# Revit family: 4C-15_Door_High_Units_FL.rfa
name_source: partatom
category: Specialty Equipment
revit_build: Autodesk Revit 2016 (Build: 20150714_1515(x64)
units: mm (PartAtom-declared; Revit-internal decimal feet)

## family parameters
Always vertical = Yes
Cut with Voids When Loaded = No
Host = Wall
Part Type = Normal
Room Calculation Point = No
Round Connector Dimension = Use Diameter
Shared = No

## types (20) — shared parameters
Assembly Code = C1030910
Back Enclosure Material = Aluminum - Salsbury Finish = Anodized
Depth = 17.025"
Height = 54.970"
Latch Locks - Left Side = No
Latch Locks - Right Side = No
Lock Material = Stainless Steel -Salsbury Finish =  Polished
Manufacturer = Salsbury Industries
MasterFormat Number = 10 55 00
MasterFormat Title = Postal Specialties
Version = 2.0 (08/09/16)

## per-type parameters (varying)
- 3715S-09 FL: Bottom Back Plate=No; Description=15 Door High Unit: 9 MB1, 1 PL4, OM2; Door Slot L1=3700 Series 4C Door Configurations : Empty; Door Slot L10=3700 Series 4C Door Configurations : Empty; Door Slot L11=3700 Series 4C Door Configurations : Empty; Door Slot L12=3700 Series 4C Door Configurations : Empty; Door Slot L13=3700 Series 4C Door Configurations : Empty; Door Slot L14=3700 Series 4C Door Configurations : Empty; Door Slot L15=3700 Series 4C Door Configurations : Empty; Door Slot L2=3700 Series 4C Door Configurations : Empty; Door Slot L3=3700 Series 4C Door Configurations : Empty; Door Slot L4=3700 Series 4C Door Configurations : Empty; Door Slot L5=3700 Series 4C Door Configurations : Empty; Door Slot L6=3700 Series 4C Door Configurations : Empty; Door Slot L7=3700 Series 4C Door Configurations : Empty; Door Slot L8=3700 Series 4C Door Configurations : Empty; Door Slot L9=3700 Series 4C Door Configurations : Empty; Door Slot R1=3700 Series 4C Door Configurations : MB1 Door; Door Slot R10=3700 Series 4C Door Configurations : MB1 Door w/ Divider; Door Slot R11=3700 Series 4C Door Configurations : MB1 Door w/ Divider; Door Slot R12=3700 Series 4C Door Configurations : Empty; Door Slot R13=3700 Series 4C Door Configurations : Empty; Door Slot R14=3700 Series 4C Door Configurations : Empty; Door Slot R15=3700 Series 4C Parcel Configurations : PL4 w/ Divider; Door Slot R2=3700 Series 4C Door Configurations : MB1 Door w/ Divider; Door Slot R3=3700 Series 4C Door Configurations : MB1 Door w/ Divider; Door Slot R4=3700 Series 4C Door Configurations : MB1 Door w/ Divider; Door Slot R5=3700 Series 4C Door Configurations : MB1 Door w/ Divider; Door Slot R6=3700 Series 4C Door Configurations : Empty; Door Slot R7=3700 Series 4C OM2 Configuration : OM2-FL; Door Slot R8=3700 Series 4C Door Configurations : MB1 Door w/ Divider; Door Slot R9=3700 Series 4C Door Configurations : MB1 Door w/ Divider; Latch Alignment=13.876"; Left Inside Wall=No; Right Inside Wall=No; Top Back Plate=No; Type Comments=4C Standard Horizontal Mailbox - Front Loading; Vertical Center Divider=No; Width=16.344"
- 3715D-20 FL: Bottom Back Plate=Yes; Description=15 Door High Unit: 20 MB1, 2 PL4, OM2; Door Slot L1=3700 Series 4C Door Configurations : MB1 Door; Door Slot L10=3700 Series 4C Door Configurations : MB1 Door w/ Divider; Door Slot L11=3700 Series 4C Door Configurations : MB1 Door w/ Divider; Door Slot L12=3700 Series 4C Door Configurations : Empty; Door Slot L13=3700 Series 4C Door Configurations : Empty; Door Slot L14=3700 Series 4C Door Configurations : Empty; Door Slot L15=3700 Series 4C Parcel Configurations : PL4 w/ Divider; Door Slot L2=3700 Series 4C Door Configurations : MB1 Door w/ Divider; Door Slot L3=3700 Series 4C Door Configurations : MB1 Door w/ Divider; Door Slot L4=3700 Series 4C Door Configurations : MB1 Door w/ Divider; Door Slot L5=3700 Series 4C Door Configurations : MB1 Door w/ Divider; Door Slot L6=3700 Series 4C Door Configurations : MB1 Door w/ Divider; Door Slot L7=3700 Series 4C Door Configurations : MB1 Door w/ Divider; Door Slot L8=3700 Series 4C Door Configurations : MB1 Door w/ Divider; Door Slot L9=3700 Series 4C Door Configurations : MB1 Door w/ Divider; Door Slot R1=3700 Series 4C Door Configurations : MB1 Door; Door Slot R10=3700 Series 4C Door Configurations : MB1 Door w/ Divider; Door Slot R11=3700 Series 4C Door Configurations : MB1 Door w/ Divider; Door Slot R12=3700 Series 4C Door Configurations : Empty; Door Slot R13=3700 Series 4C Door Configurations : Empty; Door Slot R14=3700 Series 4C Door Configurations : Empty; Door Slot R15=3700 Series 4C Parcel Configurations : PL4 w/ Divider; Door Slot R2=3700 Series 4C Door Configurations : MB1 Door w/ Divider; Door Slot R3=3700 Series 4C Door Configurations : MB1 Door w/ Divider; Door Slot R4=3700 Series 4C Door Configurations : MB1 Door w/ Divider; Door Slot R5=3700 Series 4C Door Configurations : MB1 Door w/ Divider; Door Slot R6=3700 Series 4C Door Configurations : Empty; Door Slot R7=3700 Series 4C OM2 Configuration : OM2-FL; Door Slot R8=3700 Series 4C Door Configurations : MB1 Door w/ Divider; Door Slot R9=3700 Series 4C Door Configurations : MB1 Door w/ Divider; Latch Alignment=14.857"; Left Inside Wall=Yes; Right Inside Wall=Yes; Top Back Plate=Yes; Type Comments=4C Standard Horizontal Mailbox - Front Loading; Vertical Center Divider=Yes; Width=31.098"
- 3715D-19 FL: Bottom Back Plate=Yes; Description=15 Door High Unit: 19 MB1, 1 PL4, 1 PL5, OM2; Door Slot L1=3700 Series 4C Door Configurations : MB1 Door; Door Slot L10=3700 Series 4C Door Configurations : MB1 Door w/ Divider; Door Slot L11=3700 Series 4C Door Configurations : Empty; Door Slot L12=3700 Series 4C Door Configurations : Empty; Door Slot L13=3700 Series 4C Door Configurations : Empty; Door Slot L14=3700 Series 4C Door Configurations : Empty; Door Slot L15=3700 Series 4C Parcel Configurations : PL5 w/ Divider; Door Slot L2=3700 Series 4C Door Configurations : MB1 Door w/ Divider; Door Slot L3=3700 Series 4C Door Configurations : MB1 Door w/ Divider; Door Slot L4=3700 Series 4C Door Configurations : MB1 Door w/ Divider; Door Slot L5=3700 Series 4C Door Configurations : MB1 Door w/ Divider; Door Slot L6=3700 Series 4C Door Configurations : MB1 Door w/ Divider; Door Slot L7=3700 Series 4C Door Configurations : MB1 Door w/ Divider; Door Slot L8=3700 Series 4C Door Configurations : MB1 Door w/ Divider; Door Slot L9=3700 Series 4C Door Configurations : MB1 Door w/ Divider; Door Slot R1=3700 Series 4C Door Configurations : MB1 Door; Door Slot R10=3700 Series 4C Door Configurations : MB1 Door w/ Divider; Door Slot R11=3700 Series 4C Door Configurations : MB1 Door w/ Divider; Door Slot R12=3700 Series 4C Door Configurations : Empty; Door Slot R13=3700 Series 4C Door Configurations : Empty; Door Slot R14=3700 Series 4C Door Configurations : Empty; Door Slot R15=3700 Series 4C Parcel Configurations : PL4 w/ Divider; Door Slot R2=3700 Series 4C Door Configurations : MB1 Door w/ Divider; Door Slot R3=3700 Series 4C Door Configurations : MB1 Door w/ Divider; Door Slot R4=3700 Series 4C Door Configurations : MB1 Door w/ Divider; Door Slot R5=3700 Series 4C Door Configurations : MB1 Door w/ Divider; Door Slot R6=3700 Series 4C Door Configurations : Empty; Door Slot R7=3700 Series 4C OM2 Configuration : OM2-FL; Door Slot R8=3700 Series 4C Door Configurations : MB1 Door w/ Divider; Door Slot R9=3700 Series 4C Door Configurations : MB1 Door w/ Divider; Latch Alignment=14.857"; Left Inside Wall=Yes; Right Inside Wall=Yes; Top Back Plate=Yes; Type Comments=4C Standard Horizontal Mailbox - Front Loading; Vertical Center Divider=Yes; Width=31.098"
- 3715D-18 FL: Bottom Back Plate=Yes; Description=15 Door High Unit: 18 MB1, 2 PL5, OM2; Door Slot L1=3700 Series 4C Door Configurations : MB1 Door; Door Slot L10=3700 Series 4C Door Configurations : MB1 Door w/ Divider; Door Slot L11=3700 Series 4C Door Configurations : Empty; Door Slot L12=3700 Series 4C Door Configurations : Empty; Door Slot L13=3700 Series 4C Door Configurations : Empty; Door Slot L14=3700 Series 4C Door Configurations : Empty; Door Slot L15=3700 Series 4C Parcel Configurations : PL5 w/ Divider; Door Slot L2=3700 Series 4C Door Configurations : MB1 Door w/ Divider; Door Slot L3=3700 Series 4C Door Configurations : MB1 Door w/ Divider; Door Slot L4=3700 Series 4C Door Configurations : MB1 Door w/ Divider; Door Slot L5=3700 Series 4C Door Configurations : MB1 Door w/ Divider; Door Slot L6=3700 Series 4C Door Configurations : MB1 Door w/ Divider; Door Slot L7=3700 Series 4C Door Configurations : MB1 Door w/ Divider; Door Slot L8=3700 Series 4C Door Configurations : MB1 Door w/ Divider; Door Slot L9=3700 Series 4C Door Configurations : MB1 Door w/ Divider; Door Slot R1=3700 Series 4C Door Configurations : MB1 Door; Door Slot R10=3700 Series 4C Door Configurations : MB1 Door w/ Divider; Door Slot R11=3700 Series 4C Door Configurations : Empty; Door Slot R12=3700 Series 4C Door Configurations : Empty; Door Slot R13=3700 Series 4C Door Configurations : Empty; Door Slot R14=3700 Series 4C Door Configurations : Empty; Door Slot R15=3700 Series 4C Parcel Configurations : PL5 w/ Divider; Door Slot R2=3700 Series 4C Door Configurations : MB1 Door w/ Divider; Door Slot R3=3700 Series 4C Door Configurations : MB1 Door w/ Divider; Door Slot R4=3700 Series 4C Door Configurations : MB1 Door w/ Divider; Door Slot R5=3700 Series 4C Door Configurations : MB1 Door w/ Divider; Door Slot R6=3700 Series 4C Door Configurations : Empty; Door Slot R7=3700 Series 4C OM2 Configuration : OM2-FL; Door Slot R8=3700 Series 4C Door Configurations : MB1 Door w/ Divider; Door Slot R9=3700 Series 4C Door Configurations : MB1 Door w/ Divider; Latch Alignment=14.857"; Left Inside Wall=Yes; Right Inside Wall=Yes; Top Back Plate=Yes; Type Comments=4C Standard Horizontal Mailbox - Front Loading; Vertical Center Divider=Yes; Width=31.098"
- 3715D-17 FL: Bottom Back Plate=Yes; Description=15 Door High Unit: 17 MB1, 1 PL5, 1 PL6, OM2; Door Slot L1=3700 Series 4C Door Configurations : MB1 Door; Door Slot L10=3700 Series 4C Door Configurations : Empty; Door Slot L11=3700 Series 4C Door Configurations : Empty; Door Slot L12=3700 Series 4C Door Configurations : Empty; Door Slot L13=3700 Series 4C Door Configurations : Empty; Door Slot L14=3700 Series 4C Door Configurations : Empty; Door Slot L15=3700 Series 4C Parcel Configurations : PL6 w/ Divider; Door Slot L2=3700 Series 4C Door Configurations : MB1 Door w/ Divider; Door Slot L3=3700 Series 4C Door Configurations : MB1 Door w/ Divider; Door Slot L4=3700 Series 4C Door Configurations : MB1 Door w/ Divider; Door Slot L5=3700 Series 4C Door Configurations : MB1 Door w/ Divider; Door Slot L6=3700 Series 4C Door Configurations : MB1 Door w/ Divider; Door Slot L7=3700 Series 4C Door Configurations : MB1 Door w/ Divider; Door Slot L8=3700 Series 4C Door Configurations : MB1 Door w/ Divider; Door Slot L9=3700 Series 4C Door Configurations : MB1 Door w/ Divider; Door Slot R1=3700 Series 4C Door Configurations : MB1 Door; Door Slot R10=3700 Series 4C Door Configurations : MB1 Door w/ Divider; Door Slot R11=3700 Series 4C Door Configurations : Empty; Door Slot R12=3700 Series 4C Door Configurations : Empty; Door Slot R13=3700 Series 4C Door Configurations : Empty; Door Slot R14=3700 Series 4C Door Configurations : Empty; Door Slot R15=3700 Series 4C Parcel Configurations : PL5 w/ Divider; Door Slot R2=3700 Series 4C Door Configurations : MB1 Door w/ Divider; Door Slot R3=3700 Series 4C Door Configurations : MB1 Door w/ Divider; Door Slot R4=3700 Series 4C Door Configurations : MB1 Door w/ Divider; Door Slot R5=3700 Series 4C Door Configurations : MB1 Door w/ Divider; Door Slot R6=3700 Series 4C Door Configurations : Empty; Door Slot R7=3700 Series 4C OM2 Configuration : OM2-FL; Door Slot R8=3700 Series 4C Door Configurations : MB1 Door w/ Divider; Door Slot R9=3700 Series 4C Door Configurations : MB1 Door w/ Divider; Latch Alignment=14.857"; Left Inside Wall=Yes; Right Inside Wall=Yes; Top Back Plate=Yes; Type Comments=4C Standard Horizontal Mailbox - Front Loading; Vertical Center Divider=Yes; Width=31.098"
- 3715D-16 FL: Bottom Back Plate=Yes; Description=15 Door High Unit: 16 MB1, 2 PL6, OM2; Door Slot L1=3700 Series 4C Door Configurations : MB1 Door; Door Slot L10=3700 Series 4C Door Configurations : Empty; Door Slot L11=3700 Series 4C Door Configurations : Empty; Door Slot L12=3700 Series 4C Door Configurations : Empty; Door Slot L13=3700 Series 4C Door Configurations : Empty; Door Slot L14=3700 Series 4C Door Configurations : Empty; Door Slot L15=3700 Series 4C Parcel Configurations : PL6 w/ Divider; Door Slot L2=3700 Series 4C Door Configurations : MB1 Door w/ Divider; Door Slot L3=3700 Series 4C Door Configurations : MB1 Door w/ Divider; Door Slot L4=3700 Series 4C Door Configurations : MB1 Door w/ Divider; Door Slot L5=3700 Series 4C Door Configurations : MB1 Door w/ Divider; Door Slot L6=3700 Series 4C Door Configurations : MB1 Door w/ Divider; Door Slot L7=3700 Series 4C Door Configurations : MB1 Door w/ Divider; Door Slot L8=3700 Series 4C Door Configurations : MB1 Door w/ Divider; Door Slot L9=3700 Series 4C Door Configurations : MB1 Door w/ Divider; Door Slot R1=3700 Series 4C Door Configurations : MB1 Door; Door Slot R10=3700 Series 4C Door Configurations : Empty; Door Slot R11=3700 Series 4C Door Configurations : Empty; Door Slot R12=3700 Series 4C Door Configurations : Empty; Door Slot R13=3700 Series 4C Door Configurations : Empty; Door Slot R14=3700 Series 4C Door Configurations : Empty; Door Slot R15=3700 Series 4C Parcel Configurations : PL6 w/ Divider; Door Slot R2=3700 Series 4C Door Configurations : MB1 Door w/ Divider; Door Slot R3=3700 Series 4C Door Configurations : MB1 Door w/ Divider; Door Slot R4=3700 Series 4C Door Configurations : MB1 Door w/ Divider; Door Slot R5=3700 Series 4C Door Configurations : MB1 Door w/ Divider; Door Slot R6=3700 Series 4C Door Configurations : Empty; Door Slot R7=3700 Series 4C OM2 Configuration : OM2-FL; Door Slot R8=3700 Series 4C Door Configurations : MB1 Door w/ Divider; Door Slot R9=3700 Series 4C Door Configurations : MB1 Door w/ Divider; Latch Alignment=14.857"; Left Inside Wall=Yes; Right Inside Wall=Yes; Top Back Plate=Yes; Type Comments=4C Standard Horizontal Mailbox - Front Loading; Vertical Center Divider=Yes; Width=31.098"
- 3715D-15 FL: Bottom Back Plate=Yes; Description=15 Door High Unit: 15 MB1, 2 PL6, OM3; Door Slot L1=3700 Series 4C Door Configurations : MB1 Door; Door Slot L10=3700 Series 4C Door Configurations : Empty; Door Slot L11=3700 Series 4C Door Configurations : Empty; Door Slot L12=3700 Series 4C Door Configurations : Empty; Door Slot L13=3700 Series 4C Door Configurations : Empty; Door Slot L14=3700 Series 4C Door Configurations : Empty; Door Slot L15=3700 Series 4C Parcel Configurations : PL6 w/ Divider; Door Slot L2=3700 Series 4C Door Configurations : MB1 Door w/ Divider; Door Slot L3=3700 Series 4C Door Configurations : MB1 Door w/ Divider; Door Slot L4=3700 Series 4C Door Configurations : MB1 Door w/ Divider; Door Slot L5=3700 Series 4C Door Configurations : MB1 Door w/ Divider; Door Slot L6=3700 Series 4C Door Configurations : MB1 Door w/ Divider; Door Slot L7=3700 Series 4C Door Configurations : MB1 Door w/ Divider; Door Slot L8=3700 Series 4C Door Configurations : MB1 Door w/ Divider; Door Slot L9=3700 Series 4C Door Configurations : MB1 Door w/ Divider; Door Slot R1=3700 Series 4C Door Configurations : MB1 Door; Door Slot R10=3700 Series 4C Door Configurations : Empty; Door Slot R11=3700 Series 4C Door Configurations : Empty; Door Slot R12=3700 Series 4C Door Configurations : Empty; Door Slot R13=3700 Series 4C Door Configurations : Empty; Door Slot R14=3700 Series 4C Door Configurations : Empty; Door Slot R15=3700 Series 4C Parcel Configurations : PL6 w/ Divider; Door Slot R2=3700 Series 4C Door Configurations : MB1 Door w/ Divider; Door Slot R3=3700 Series 4C Door Configurations : MB1 Door w/ Divider; Door Slot R4=3700 Series 4C Door Configurations : MB1 Door w/ Divider; Door Slot R5=3700 Series 4C Door Configurations : MB1 Door w/ Divider; Door Slot R6=3700 Series 4C Door Configurations : Empty; Door Slot R7=3700 Series 4C Door Configurations : Empty; Door Slot R8=3700 Series 4C OM3 Configuration : OM3-FL; Door Slot R9=3700 Series 4C Door Configurations : MB1 Door w/ Divider; Latch Alignment=14.857"; Left Inside Wall=Yes; Right Inside Wall=Yes; Top Back Plate=Yes; Type Comments=4C Standard Horizontal Mailbox - Front Loading; Vertical Center Divider=Yes; Width=31.098"
- 3715D-09 FL: Bottom Back Plate=Yes; Description=15 Door High Unit: 9 MB2, 2 PL5, OM2; Door Slot L1=3700 Series 4C Door Configurations : Empty; Door Slot L10=3700 Series 4C Door Configurations : MB2 Door w/ Divider; Door Slot L11=3700 Series 4C Door Configurations : Empty; Door Slot L12=3700 Series 4C Door Configurations : Empty; Door Slot L13=3700 Series 4C Door Configurations : Empty; Door Slot L14=3700 Series 4C Door Configurations : Empty; Door Slot L15=3700 Series 4C Parcel Configurations : PL5 w/ Divider; Door Slot L2=3700 Series 4C Door Configurations : MB2 Door; Door Slot L3=3700 Series 4C Door Configurations : Empty; Door Slot L4=3700 Series 4C Door Configurations : MB2 Door w/ Divider; Door Slot L5=3700 Series 4C Door Configurations : Empty; Door Slot L6=3700 Series 4C Door Configurations : MB2 Door w/ Divider; Door Slot L7=3700 Series 4C Door Configurations : Empty; Door Slot L8=3700 Series 4C Door Configurations : MB2 Door w/ Divider; Door Slot L9=3700 Series 4C Door Configurations : Empty; Door Slot R1=3700 Series 4C Door Configurations : Empty; Door Slot R10=3700 Series 4C Door Configurations : MB2 Door w/ Divider; Door Slot R11=3700 Series 4C Door Configurations : Empty; Door Slot R12=3700 Series 4C Door Configurations : Empty; Door Slot R13=3700 Series 4C Door Configurations : Empty; Door Slot R14=3700 Series 4C Door Configurations : Empty; Door Slot R15=3700 Series 4C Parcel Configurations : PL5 w/ Divider; Door Slot R2=3700 Series 4C Door Configurations : MB2 Door; Door Slot R3=3700 Series 4C Door Configurations : Empty; Door Slot R4=3700 Series 4C Door Configurations : MB2 Door w/ Divider; Door Slot R5=3700 Series 4C Door Configurations : Empty; Door Slot R6=3700 Series 4C Door Configurations : MB2 Door w/ Divider; Door Slot R7=3700 Series 4C Door Configurations : Empty; Door Slot R8=3700 Series 4C OM2 Configuration : OM2-FL; Door Slot R9=3700 Series 4C Door Configurations : Empty; Latch Alignment=14.857"; Left Inside Wall=Yes; Right Inside Wall=Yes; Top Back Plate=Yes; Type Comments=4C Standard Horizontal Mailbox - Front Loading; Vertical Center Divider=Yes; Width=31.098"
- 3715S-08 FL: Bottom Back Plate=No; Description=15 Door High Unit: 8 MB1, 1 PL5, OM2; Door Slot L1=3700 Series 4C Door Configurations : Empty; Door Slot L10=3700 Series 4C Door Configurations : Empty; Door Slot L11=3700 Series 4C Door Configurations : Empty; Door Slot L12=3700 Series 4C Door Configurations : Empty; Door Slot L13=3700 Series 4C Door Configurations : Empty; Door Slot L14=3700 Series 4C Door Configurations : Empty; Door Slot L15=3700 Series 4C Door Configurations : Empty; Door Slot L2=3700 Series 4C Door Configurations : Empty; Door Slot L3=3700 Series 4C Door Configurations : Empty; Door Slot L4=3700 Series 4C Door Configurations : Empty; Door Slot L5=3700 Series 4C Door Configurations : Empty; Door Slot L6=3700 Series 4C Door Configurations : Empty; Door Slot L7=3700 Series 4C Door Configurations : Empty; Door Slot L8=3700 Series 4C Door Configurations : Empty; Door Slot L9=3700 Series 4C Door Configurations : Empty; Door Slot R1=3700 Series 4C Door Configurations : MB1 Door; Door Slot R10=3700 Series 4C Door Configurations : MB1 Door w/ Divider; Door Slot R11=3700 Series 4C Door Configurations : Empty; Door Slot R12=3700 Series 4C Door Configurations : Empty; Door Slot R13=3700 Series 4C Door Configurations : Empty; Door Slot R14=3700 Series 4C Door Configurations : Empty; Door Slot R15=3700 Series 4C Parcel Configurations : PL5 w/ Divider; Door Slot R2=3700 Series 4C Door Configurations : MB1 Door w/ Divider; Door Slot R3=3700 Series 4C Door Configurations : MB1 Door w/ Divider; Door Slot R4=3700 Series 4C Door Configurations : MB1 Door w/ Divider; Door Slot R5=3700 Series 4C Door Configurations : MB1 Door w/ Divider; Door Slot R6=3700 Series 4C Door Configurations : Empty; Door Slot R7=3700 Series 4C OM2 Configuration : OM2-FL; Door Slot R8=3700 Series 4C Door Configurations : MB1 Door w/ Divider; Door Slot R9=3700 Series 4C Door Configurations : MB1 Door w/ Divider; Latch Alignment=13.876"; Left Inside Wall=No; Right Inside Wall=No; Top Back Plate=No; Type Comments=4C Standard Horizontal Mailbox - Front Loading; Vertical Center Divider=No; Width=16.344"
- 3715S-07 FL: Bottom Back Plate=No; Description=15 Door High Unit: 7 MB1, 1 PL6, OM2; Door Slot L1=3700 Series 4C Door Configurations : Empty; Door Slot L10=3700 Series 4C Door Configurations : Empty; Door Slot L11=3700 Series 4C Door Configurations : Empty; Door Slot L12=3700 Series 4C Door Configurations : Empty; Door Slot L13=3700 Series 4C Door Configurations : Empty; Door Slot L14=3700 Series 4C Door Configurations : Empty; Door Slot L15=3700 Series 4C Door Configurations : Empty; Door Slot L2=3700 Series 4C Door Configurations : Empty; Door Slot L3=3700 Series 4C Door Configurations : Empty; Door Slot L4=3700 Series 4C Door Configurations : Empty; Door Slot L5=3700 Series 4C Door Configurations : Empty; Door Slot L6=3700 Series 4C Door Configurations : Empty; Door Slot L7=3700 Series 4C Door Configurations : Empty; Door Slot L8=3700 Series 4C Door Configurations : Empty; Door Slot L9=3700 Series 4C Door Configurations : Empty; Door Slot R1=3700 Series 4C Door Configurations : MB1 Door; Door Slot R10=3700 Series 4C Door Configurations : Empty; Door Slot R11=3700 Series 4C Door Configurations : Empty; Door Slot R12=3700 Series 4C Door Configurations : Empty; Door Slot R13=3700 Series 4C Door Configurations : Empty; Door Slot R14=3700 Series 4C Door Configurations : Empty; Door Slot R15=3700 Series 4C Parcel Configurations : PL6 w/ Divider; Door Slot R2=3700 Series 4C Door Configurations : MB1 Door w/ Divider; Door Slot R3=3700 Series 4C Door Configurations : MB1 Door w/ Divider; Door Slot R4=3700 Series 4C Door Configurations : MB1 Door w/ Divider; Door Slot R5=3700 Series 4C Door Configurations : MB1 Door w/ Divider; Door Slot R6=3700 Series 4C Door Configurations : Empty; Door Slot R7=3700 Series 4C OM2 Configuration : OM2-FL; Door Slot R8=3700 Series 4C Door Configurations : MB1 Door w/ Divider; Door Slot R9=3700 Series 4C Door Configurations : MB1 Door w/ Divider; Latch Alignment=13.876"; Left Inside Wall=No; Right Inside Wall=No; Top Back Plate=No; Type Comments=4C Standard Horizontal Mailbox - Front Loading; Vertical Center Divider=No; Width=16.344"
- 3715S-06 FL: Bottom Back Plate=No; Description=15 Door High Unit: 6 MB1, 1 PL6, OM3; Door Slot L1=3700 Series 4C Door Configurations : Empty; Door Slot L10=3700 Series 4C Door Configurations : Empty; Door Slot L11=3700 Series 4C Door Configurations : Empty; Door Slot L12=3700 Series 4C Door Configurations : Empty; Door Slot L13=3700 Series 4C Door Configurations : Empty; Door Slot L14=3700 Series 4C Door Configurations : Empty; Door Slot L15=3700 Series 4C Door Configurations : Empty; Door Slot L2=3700 Series 4C Door Configurations : Empty; Door Slot L3=3700 Series 4C Door Configurations : Empty; Door Slot L4=3700 Series 4C Door Configurations : Empty; Door Slot L5=3700 Series 4C Door Configurations : Empty; Door Slot L6=3700 Series 4C Door Configurations : Empty; Door Slot L7=3700 Series 4C Door Configurations : Empty; Door Slot L8=3700 Series 4C Door Configurations : Empty; Door Slot L9=3700 Series 4C Door Configurations : Empty; Door Slot R1=3700 Series 4C Door Configurations : MB1 Door; Door Slot R10=3700 Series 4C Door Configurations : Empty; Door Slot R11=3700 Series 4C Door Configurations : Empty; Door Slot R12=3700 Series 4C Door Configurations : Empty; Door Slot R13=3700 Series 4C Door Configurations : Empty; Door Slot R14=3700 Series 4C Door Configurations : Empty; Door Slot R15=3700 Series 4C Parcel Configurations : PL6 w/ Divider; Door Slot R2=3700 Series 4C Door Configurations : MB1 Door w/ Divider; Door Slot R3=3700 Series 4C Door Configurations : MB1 Door w/ Divider; Door Slot R4=3700 Series 4C Door Configurations : MB1 Door w/ Divider; Door Slot R5=3700 Series 4C Door Configurations : MB1 Door w/ Divider; Door Slot R6=3700 Series 4C Door Configurations : Empty; Door Slot R7=3700 Series 4C Door Configurations : Empty; Door Slot R8=3700 Series 4C OM3 Configuration : OM3-FL; Door Slot R9=3700 Series 4C Door Configurations : MB1 Door w/ Divider; Latch Alignment=13.876"; Left Inside Wall=No; Right Inside Wall=No; Top Back Plate=No; Type Comments=4C Standard Horizontal Mailbox - Front Loading; Vertical Center Divider=No; Width=16.344"
- 3715S-04 FL: Bottom Back Plate=No; Description=15 Door High Unit: 4 MB2, 1 PL5, OM2; Door Slot L1=3700 Series 4C Door Configurations : Empty; Door Slot L10=3700 Series 4C Door Configurations : Empty; Door Slot L11=3700 Series 4C Door Configurations : Empty; Door Slot L12=3700 Series 4C Door Configurations : Empty; Door Slot L13=3700 Series 4C Door Configurations : Empty; Door Slot L14=3700 Series 4C Door Configurations : Empty; Door Slot L15=3700 Series 4C Door Configurations : Empty; Door Slot L2=3700 Series 4C Door Configurations : Empty; Door Slot L3=3700 Series 4C Door Configurations : Empty; Door Slot L4=3700 Series 4C Door Configurations : Empty; Door Slot L5=3700 Series 4C Door Configurations : Empty; Door Slot L6=3700 Series 4C Door Configurations : Empty; Door Slot L7=3700 Series 4C Door Configurations : Empty; Door Slot L8=3700 Series 4C Door Configurations : Empty; Door Slot L9=3700 Series 4C Door Configurations : Empty; Door Slot R1=3700 Series 4C Door Configurations : Empty; Door Slot R10=3700 Series 4C Door Configurations : MB2 Door w/ Divider; Door Slot R11=3700 Series 4C Door Configurations : Empty; Door Slot R12=3700 Series 4C Door Configurations : Empty; Door Slot R13=3700 Series 4C Door Configurations : Empty; Door Slot R14=3700 Series 4C Door Configurations : Empty; Door Slot R15=3700 Series 4C Parcel Configurations : PL5 w/ Divider; Door Slot R2=3700 Series 4C Door Configurations : MB2 Door; Door Slot R3=3700 Series 4C Door Configurations : Empty; Door Slot R4=3700 Series 4C Door Configurations : MB2 Door w/ Divider; Door Slot R5=3700 Series 4C Door Configurations : Empty; Door Slot R6=3700 Series 4C Door Configurations : MB2 Door w/ Divider; Door Slot R7=3700 Series 4C Door Configurations : Empty; Door Slot R8=3700 Series 4C OM2 Configuration : OM2-FL; Door Slot R9=3700 Series 4C Door Configurations : Empty; Latch Alignment=13.876"; Left Inside Wall=No; Right Inside Wall=No; Top Back Plate=No; Type Comments=4C Standard Horizontal Mailbox - Front Loading; Vertical Center Divider=No; Width=16.344"
- 3715S-3P FL: Bottom Back Plate=No; Description=15 Door High Unit: 3 PL5; Door Slot L1=3700 Series 4C Door Configurations : Empty; Door Slot L10=3700 Series 4C Door Configurations : Empty; Door Slot L11=3700 Series 4C Door Configurations : Empty; Door Slot L12=3700 Series 4C Door Configurations : Empty; Door Slot L13=3700 Series 4C Door Configurations : Empty; Door Slot L14=3700 Series 4C Door Configurations : Empty; Door Slot L15=3700 Series 4C Door Configurations : Empty; Door Slot L2=3700 Series 4C Door Configurations : Empty; Door Slot L3=3700 Series 4C Door Configurations : Empty; Door Slot L4=3700 Series 4C Door Configurations : Empty; Door Slot L5=3700 Series 4C Door Configurations : Empty; Door Slot L6=3700 Series 4C Door Configurations : Empty; Door Slot L7=3700 Series 4C Door Configurations : Empty; Door Slot L8=3700 Series 4C Door Configurations : Empty; Door Slot L9=3700 Series 4C Door Configurations : Empty; Door Slot R1=3700 Series 4C Door Configurations : Empty; Door Slot R10=3700 Series 4C Parcel Configurations : PL5 w/ Divider; Door Slot R11=3700 Series 4C Door Configurations : Empty; Door Slot R12=3700 Series 4C Door Configurations : Empty; Door Slot R13=3700 Series 4C Door Configurations : Empty; Door Slot R14=3700 Series 4C Door Configurations : Empty; Door Slot R15=3700 Series 4C Parcel Configurations : PL5 w/ Divider; Door Slot R2=3700 Series 4C Door Configurations : Empty; Door Slot R3=3700 Series 4C Door Configurations : Empty; Door Slot R4=3700 Series 4C Door Configurations : Empty; Door Slot R5=3700 Series 4C Parcel Configurations : PL5; Door Slot R6=3700 Series 4C Door Configurations : Empty; Door Slot R7=3700 Series 4C Door Configurations : Empty; Door Slot R8=3700 Series 4C Door Configurations : Empty; Door Slot R9=3700 Series 4C Door Configurations : Empty; Latch Alignment=13.876"; Left Inside Wall=No; Right Inside Wall=No; Top Back Plate=No; Type Comments=4C Standard Horizontal Mailbox - Front Loading; Vertical Center Divider=No; Width=16.344"
- 3715D-29 FL: Bottom Back Plate=Yes; Description=15 Door High Unit: 29 MB1, CA; Door Slot L1=3700 Series 4C Door Configurations : MB1 Door; Door Slot L10=3700 Series 4C Door Configurations : MB1 Door w/ Divider; Door Slot L11=3700 Series 4C Door Configurations : MB1 Door w/ Divider; Door Slot L12=3700 Series 4C Door Configurations : MB1 Door w/ Divider; Door Slot L13=3700 Series 4C Door Configurations : MB1 Door w/ Divider; Door Slot L14=3700 Series 4C Door Configurations : MB1 Door w/ Divider; Door Slot L15=3700 Series 4C Door Configurations : MB1 Door w/ Divider; Door Slot L2=3700 Series 4C Door Configurations : MB1 Door w/ Divider; Door Slot L3=3700 Series 4C Door Configurations : MB1 Door w/ Divider; Door Slot L4=3700 Series 4C Door Configurations : MB1 Door w/ Divider; Door Slot L5=3700 Series 4C Door Configurations : MB1 Door w/ Divider; Door Slot L6=3700 Series 4C Door Configurations : MB1 Door w/ Divider; Door Slot L7=3700 Series 4C Door Configurations : MB1 Door w/ Divider; Door Slot L8=3700 Series 4C Door Configurations : MB1 Door w/ Divider; Door Slot L9=3700 Series 4C Door Configurations : MB1 Door w/ Divider; Door Slot R1=3700 Series 4C Door Configurations : MB1 Door; Door Slot R10=3700 Series 4C Door Configurations : MB1 Door w/ Divider; Door Slot R11=3700 Series 4C Door Configurations : MB1 Door w/ Divider; Door Slot R12=3700 Series 4C Door Configurations : MB1 Door w/ Divider; Door Slot R13=3700 Series 4C Door Configurations : MB1 Door w/ Divider; Door Slot R14=3700 Series 4C Door Configurations : MB1 Door w/ Divider; Door Slot R15=3700 Series 4C Door Configurations : MB1 Door w/ Divider; Door Slot R2=3700 Series 4C Door Configurations : MB1 Door w/ Divider; Door Slot R3=3700 Series 4C Door Configurations : MB1 Door w/ Divider; Door Slot R4=3700 Series 4C Door Configurations : MB1 Door w/ Divider; Door Slot R5=3700 Series 4C Door Configurations : MB1 Door w/ Divider; Door Slot R6=3700 Series 4C Door Configurations : MB1 Door w/ Divider; Door Slot R7=3700 Series 4C Door Configurations : MB1 Door w/ Divider; Door Slot R8=3700 Series 4C OM1 Configuration : OM1-FL; Door Slot R9=3700 Series 4C Door Configurations : MB1 Door w/ Divider; Latch Alignment=14.857"; Left Inside Wall=Yes; Right Inside Wall=Yes; Top Back Plate=Yes; Type Comments=4C Standard Horizontal Mailbox - Front Loading; Vertical Center Divider=Yes; Width=31.098"
- 3715D-28 FL: Bottom Back Plate=Yes; Description=15 Door High Unit: 28 MB1, OM2; Door Slot L1=3700 Series 4C Door Configurations : MB1 Door; Door Slot L10=3700 Series 4C Door Configurations : MB1 Door w/ Divider; Door Slot L11=3700 Series 4C Door Configurations : MB1 Door w/ Divider; Door Slot L12=3700 Series 4C Door Configurations : MB1 Door w/ Divider; Door Slot L13=3700 Series 4C Door Configurations : MB1 Door w/ Divider; Door Slot L14=3700 Series 4C Door Configurations : MB1 Door w/ Divider; Door Slot L15=3700 Series 4C Door Configurations : MB1 Door w/ Divider; Door Slot L2=3700 Series 4C Door Configurations : MB1 Door w/ Divider; Door Slot L3=3700 Series 4C Door Configurations : MB1 Door w/ Divider; Door Slot L4=3700 Series 4C Door Configurations : MB1 Door w/ Divider; Door Slot L5=3700 Series 4C Door Configurations : MB1 Door w/ Divider; Door Slot L6=3700 Series 4C Door Configurations : MB1 Door w/ Divider; Door Slot L7=3700 Series 4C Door Configurations : MB1 Door w/ Divider; Door Slot L8=3700 Series 4C Door Configurations : MB1 Door w/ Divider; Door Slot L9=3700 Series 4C Door Configurations : MB1 Door w/ Divider; Door Slot R1=3700 Series 4C Door Configurations : MB1 Door; Door Slot R10=3700 Series 4C Door Configurations : MB1 Door w/ Divider; Door Slot R11=3700 Series 4C Door Configurations : MB1 Door w/ Divider; Door Slot R12=3700 Series 4C Door Configurations : MB1 Door w/ Divider; Door Slot R13=3700 Series 4C Door Configurations : MB1 Door w/ Divider; Door Slot R14=3700 Series 4C Door Configurations : MB1 Door w/ Divider; Door Slot R15=3700 Series 4C Door Configurations : MB1 Door w/ Divider; Door Slot R2=3700 Series 4C Door Configurations : MB1 Door w/ Divider; Door Slot R3=3700 Series 4C Door Configurations : MB1 Door w/ Divider; Door Slot R4=3700 Series 4C Door Configurations : MB1 Door w/ Divider; Door Slot R5=3700 Series 4C Door Configurations : MB1 Door w/ Divider; Door Slot R6=3700 Series 4C Door Configurations : MB1 Door w/ Divider; Door Slot R7=3700 Series 4C Door Configurations : Empty; Door Slot R8=3700 Series 4C OM2 Configuration : OM2-FL; Door Slot R9=3700 Series 4C Door Configurations : MB1 Door w/ Divider; Latch Alignment=14.857"; Left Inside Wall=Yes; Right Inside Wall=Yes; Top Back Plate=Yes; Type Comments=4C Standard Horizontal Mailbox - Front Loading; Vertical Center Divider=Yes; Width=31.098"
- 3715D-13 FL: Bottom Back Plate=Yes; Description=15 Door High Unit: 11 MB2, 2 MB3, OM2; Door Slot L1=3700 Series 4C Door Configurations : Empty; Door Slot L10=3700 Series 4C Door Configurations : MB2 Door w/ Divider; Door Slot L11=3700 Series 4C Door Configurations : Empty; Door Slot L12=3700 Series 4C Door Configurations : MB2 Door w/ Divider; Door Slot L13=3700 Series 4C Door Configurations : Empty; Door Slot L14=3700 Series 4C Door Configurations : Empty; Door Slot L15=3700 Series 4C Door Configurations : MB3 Door w/ Divider; Door Slot L2=3700 Series 4C Door Configurations : MB2 Door; Door Slot L3=3700 Series 4C Door Configurations : Empty; Door Slot L4=3700 Series 4C Door Configurations : MB2 Door w/ Divider; Door Slot L5=3700 Series 4C Door Configurations : Empty; Door Slot L6=3700 Series 4C Door Configurations : MB2 Door w/ Divider; Door Slot L7=3700 Series 4C Door Configurations : Empty; Door Slot L8=3700 Series 4C Door Configurations : MB2 Door w/ Divider; Door Slot L9=3700 Series 4C Door Configurations : Empty; Door Slot R1=3700 Series 4C Door Configurations : Empty; Door Slot R10=3700 Series 4C Door Configurations : MB2 Door w/ Divider; Door Slot R11=3700 Series 4C Door Configurations : Empty; Door Slot R12=3700 Series 4C Door Configurations : MB2 Door w/ Divider; Door Slot R13=3700 Series 4C Door Configurations : Empty; Door Slot R14=3700 Series 4C Door Configurations : Empty; Door Slot R15=3700 Series 4C Door Configurations : MB3 Door w/ Divider; Door Slot R2=3700 Series 4C Door Configurations : MB2 Door; Door Slot R3=3700 Series 4C Door Configurations : Empty; Door Slot R4=3700 Series 4C Door Configurations : MB2 Door w/ Divider; Door Slot R5=3700 Series 4C Door Configurations : Empty; Door Slot R6=3700 Series 4C Door Configurations : MB2 Door w/ Divider; Door Slot R7=3700 Series 4C Door Configurations : Empty; Door Slot R8=3700 Series 4C OM2 Configuration : OM2-FL; Door Slot R9=3700 Series 4C Door Configurations : Empty; Latch Alignment=14.857"; Left Inside Wall=Yes; Right Inside Wall=Yes; Top Back Plate=Yes; Type Comments=4C Standard Horizontal Mailbox - Front Loading; Vertical Center Divider=Yes; Width=31.098"
- 3715S-14 FL: Bottom Back Plate=No; Description=15 Door High Unit: 14 MB1, CA; Door Slot L1=3700 Series 4C Door Configurations : Empty; Door Slot L10=3700 Series 4C Door Configurations : Empty; Door Slot L11=3700 Series 4C Door Configurations : Empty; Door Slot L12=3700 Series 4C Door Configurations : Empty; Door Slot L13=3700 Series 4C Door Configurations : Empty; Door Slot L14=3700 Series 4C Door Configurations : Empty; Door Slot L15=3700 Series 4C Door Configurations : Empty; Door Slot L2=3700 Series 4C Door Configurations : Empty; Door Slot L3=3700 Series 4C Door Configurations : Empty; Door Slot L4=3700 Series 4C Door Configurations : Empty; Door Slot L5=3700 Series 4C Door Configurations : Empty; Door Slot L6=3700 Series 4C Door Configurations : Empty; Door Slot L7=3700 Series 4C Door Configurations : Empty; Door Slot L8=3700 Series 4C Door Configurations : Empty; Door Slot L9=3700 Series 4C Door Configurations : Empty; Door Slot R1=3700 Series 4C Door Configurations : MB1 Door; Door Slot R10=3700 Series 4C Door Configurations : MB1 Door w/ Divider; Door Slot R11=3700 Series 4C Door Configurations : MB1 Door w/ Divider; Door Slot R12=3700 Series 4C Door Configurations : MB1 Door w/ Divider; Door Slot R13=3700 Series 4C Door Configurations : MB1 Door w/ Divider; Door Slot R14=3700 Series 4C Door Configurations : MB1 Door w/ Divider; Door Slot R15=3700 Series 4C Door Configurations : MB1 Door w/ Divider; Door Slot R2=3700 Series 4C Door Configurations : MB1 Door w/ Divider; Door Slot R3=3700 Series 4C Door Configurations : MB1 Door w/ Divider; Door Slot R4=3700 Series 4C Door Configurations : MB1 Door w/ Divider; Door Slot R5=3700 Series 4C Door Configurations : MB1 Door w/ Divider; Door Slot R6=3700 Series 4C Door Configurations : MB1 Door w/ Divider; Door Slot R7=3700 Series 4C Door Configurations : MB1 Door w/ Divider; Door Slot R8=3700 Series 4C OM1 Configuration : OM1-FL; Door Slot R9=3700 Series 4C Door Configurations : MB1 Door w/ Divider; Latch Alignment=13.876"; Left Inside Wall=No; Right Inside Wall=No; Top Back Plate=No; Type Comments=4C Standard Horizontal Mailbox - Front Loading; Vertical Center Divider=No; Width=16.344"
- 3715S-13 FL: Bottom Back Plate=No; Description=15 Door High Unit: 13 MB1, OM2; Door Slot L1=3700 Series 4C Door Configurations : Empty; Door Slot L10=3700 Series 4C Door Configurations : Empty; Door Slot L11=3700 Series 4C Door Configurations : Empty; Door Slot L12=3700 Series 4C Door Configurations : Empty; Door Slot L13=3700 Series 4C Door Configurations : Empty; Door Slot L14=3700 Series 4C Door Configurations : Empty; Door Slot L15=3700 Series 4C Door Configurations : Empty; Door Slot L2=3700 Series 4C Door Configurations : Empty; Door Slot L3=3700 Series 4C Door Configurations : Empty; Door Slot L4=3700 Series 4C Door Configurations : Empty; Door Slot L5=3700 Series 4C Door Configurations : Empty; Door Slot L6=3700 Series 4C Door Configurations : Empty; Door Slot L7=3700 Series 4C Door Configurations : Empty; Door Slot L8=3700 Series 4C Door Configurations : Empty; Door Slot L9=3700 Series 4C Door Configurations : Empty; Door Slot R1=3700 Series 4C Door Configurations : MB1 Door; Door Slot R10=3700 Series 4C Door Configurations : MB1 Door w/ Divider; Door Slot R11=3700 Series 4C Door Configurations : MB1 Door w/ Divider; Door Slot R12=3700 Series 4C Door Configurations : MB1 Door w/ Divider; Door Slot R13=3700 Series 4C Door Configurations : MB1 Door w/ Divider; Door Slot R14=3700 Series 4C Door Configurations : MB1 Door w/ Divider; Door Slot R15=3700 Series 4C Door Configurations : MB1 Door w/ Divider; Door Slot R2=3700 Series 4C Door Configurations : MB1 Door w/ Divider; Door Slot R3=3700 Series 4C Door Configurations : MB1 Door w/ Divider; Door Slot R4=3700 Series 4C Door Configurations : MB1 Door w/ Divider; Door Slot R5=3700 Series 4C Door Configurations : MB1 Door w/ Divider; Door Slot R6=3700 Series 4C Door Configurations : MB1 Door w/ Divider; Door Slot R7=3700 Series 4C Door Configurations : Empty; Door Slot R8=3700 Series 4C OM2 Configuration : OM2-FL; Door Slot R9=3700 Series 4C Door Configurations : MB1 Door w/ Divider; Latch Alignment=13.876"; Left Inside Wall=No; Right Inside Wall=No; Top Back Plate=No; Type Comments=4C Standard Horizontal Mailbox - Front Loading; Vertical Center Divider=No; Width=16.344"
- 3715S-1C FL: Bottom Back Plate=No; Description=15 Door High Unit; Door Slot L1=3700 Series 4C Door Configurations : Empty; Door Slot L10=3700 Series 4C Door Configurations : Empty; Door Slot L11=3700 Series 4C Door Configurations : Empty; Door Slot L12=3700 Series 4C Door Configurations : Empty; Door Slot L13=3700 Series 4C Door Configurations : Empty; Door Slot L14=3700 Series 4C Door Configurations : Empty; Door Slot L15=3700 Series 4C Door Configurations : Empty; Door Slot L2=3700 Series 4C Door Configurations : Empty; Door Slot L3=3700 Series 4C Door Configurations : Empty; Door Slot L4=3700 Series 4C Door Configurations : Empty; Door Slot L5=3700 Series 4C Door Configurations : Empty; Door Slot L6=3700 Series 4C Door Configurations : Empty; Door Slot L7=3700 Series 4C Door Configurations : Empty; Door Slot L8=3700 Series 4C Door Configurations : Empty; Door Slot L9=3700 Series 4C Door Configurations : Empty; Door Slot R1=3700 Series 4C Door Configurations : Empty; Door Slot R10=3700 Series 4C Door Configurations : Empty; Door Slot R11=3700 Series 4C Door Configurations : Empty; Door Slot R12=3700 Series 4C Door Configurations : Empty; Door Slot R13=3700 Series 4C Door Configurations : Empty; Door Slot R14=3700 Series 4C Door Configurations : Empty; Door Slot R15=4C-15 Door High Collection Box; Door Slot R2=3700 Series 4C Door Configurations : Empty; Door Slot R3=3700 Series 4C Door Configurations : Empty; Door Slot R4=3700 Series 4C Door Configurations : Empty; Door Slot R5=3700 Series 4C Door Configurations : Empty; Door Slot R6=3700 Series 4C Door Configurations : Empty; Door Slot R7=3700 Series 4C Door Configurations : Empty; Door Slot R8=3700 Series 4C Door Configurations : Empty; Door Slot R9=3700 Series 4C Door Configurations : Empty; Latch Alignment=13.876"; Left Inside Wall=No; Right Inside Wall=No; Top Back Plate=No; Type Comments=4C Horizontal Collection Box - Front Loading; Vertical Center Divider=No; Width=16.344"
- 3715S-2B FL: Bottom Back Plate=No; Description=15 Door High Unit - 2 Receptacles; Door Slot L1=3700 Series 4C Door Configurations : Empty; Door Slot L10=3700 Series 4C Door Configurations : Empty; Door Slot L11=3700 Series 4C Door Configurations : Empty; Door Slot L12=3700 Series 4C Door Configurations : Empty; Door Slot L13=3700 Series 4C Door Configurations : Empty; Door Slot L14=3700 Series 4C Door Configurations : Empty; Door Slot L15=3700 Series 4C Door Configurations : Empty; Door Slot L2=3700 Series 4C Door Configurations : Empty; Door Slot L3=3700 Series 4C Door Configurations : Empty; Door Slot L4=3700 Series 4C Door Configurations : Empty; Door Slot L5=3700 Series 4C Door Configurations : Empty; Door Slot L6=3700 Series 4C Door Configurations : Empty; Door Slot L7=3700 Series 4C Door Configurations : Empty; Door Slot L8=3700 Series 4C Door Configurations : Empty; Door Slot L9=3700 Series 4C Door Configurations : Empty; Door Slot R1=3700 Series 4C Door Configurations : Empty; Door Slot R10=3700 Series 4C Door Configurations : Empty; Door Slot R11=3700 Series 4C Door Configurations : Empty; Door Slot R12=3700 Series 4C Door Configurations : Empty; Door Slot R13=3700 Series 4C Door Configurations : Empty; Door Slot R14=3700 Series 4C Door Configurations : Empty; Door Slot R15=4C-15 Door High Receptacle; Door Slot R2=3700 Series 4C Door Configurations : Empty; Door Slot R3=3700 Series 4C Door Configurations : Empty; Door Slot R4=3700 Series 4C Door Configurations : Empty; Door Slot R5=3700 Series 4C Door Configurations : Empty; Door Slot R6=3700 Series 4C Door Configurations : Empty; Door Slot R7=3700 Series 4C Door Configurations : Empty; Door Slot R8=3700 Series 4C Door Configurations : Empty; Door Slot R9=3700 Series 4C Door Configurations : Empty; Latch Alignment=13.876"; Left Inside Wall=No; Right Inside Wall=No; Top Back Plate=No; Type Comments=4C Horizontal Receptacle Bin - Front Loading; Vertical Center Divider=No; Width=16.344"

note: column(s) folded — value = type name in every type: Model

## geometry (parser evidence)
native form markers: Blend x18, Extrusion x13, Sweep x75
no freeform markers — native parametric forms only
